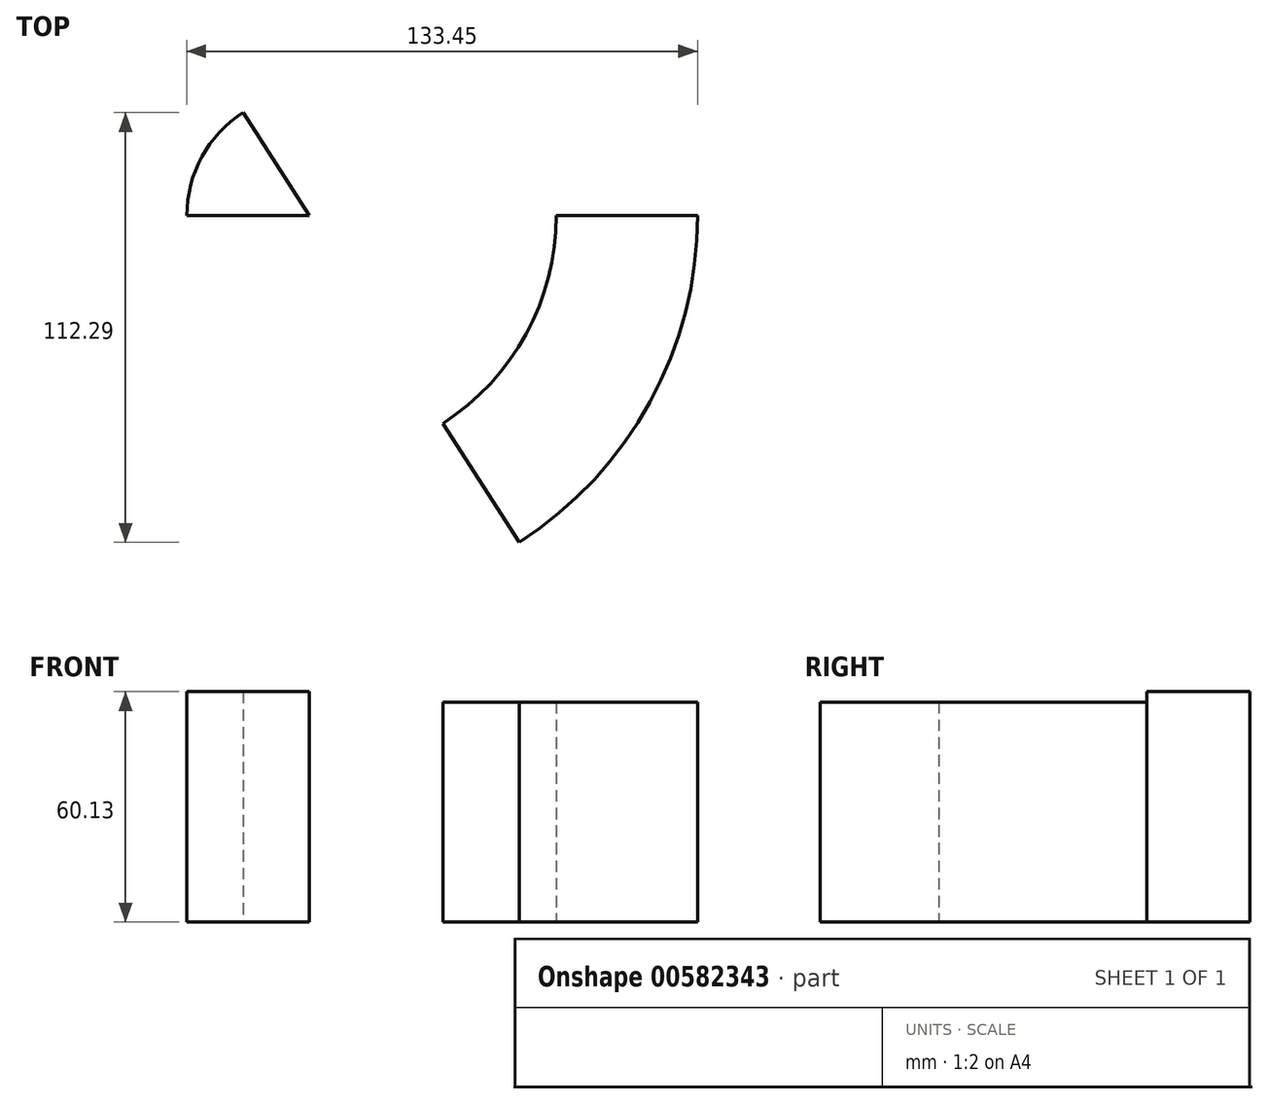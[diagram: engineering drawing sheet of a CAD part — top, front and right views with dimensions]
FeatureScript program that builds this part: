
annotation { "Feature Type Name" : "Feature", "Feature Type Description" : "" }
export const myFeature = defineFeature(function(context is Context, id is Id, definition is map)
    precondition{}
    {
        {
            var Q0;
            Q0=qCreatedBy(makeId("Front.planeOp"),FACE);
            var sketch = newSketch(context, id + "F0", { "sketchPlane" : qUnion([Q0])});
            skLineSegment(sketch, "E0.bottom", {"start": v(-61.35, 60.13) * mm, "end": v(-29.33, 60.13) * mm});
            skLineSegment(sketch, "E0.top", {"start": v(-61.35, 0) * mm, "end": v(-29.33, 0) * mm});
            skLineSegment(sketch, "E0.left", {"start": v(-61.35, 60.13) * mm, "end": v(-61.35, 0) * mm});
            skLineSegment(sketch, "E0.right", {"start": v(-29.33, 60.13) * mm, "end": v(-29.33, 0) * mm});
            skLineSegment(sketch, "E1.bottom", {"start": v(35.2, 57.44) * mm, "end": v(72.1, 57.44) * mm});
            skLineSegment(sketch, "E1.top", {"start": v(35.2, 0) * mm, "end": v(72.1, 0) * mm});
            skLineSegment(sketch, "E1.left", {"start": v(35.2, 57.44) * mm, "end": v(35.2, 0) * mm});
            skLineSegment(sketch, "E1.right", {"start": v(72.1, 57.44) * mm, "end": v(72.1, 0) * mm});
            skSolve(sketch);
        }
        {
            var Q0;
            Q0 = qSketchRegion(id + "F0", true);
            var Q1;
            Q1=sQuery(id+"F0.wireOp",EDGE,"E0.right");
            revolve(context, id + "F1", {"entities" : qUnion([Q0]), "axis" : qUnion([Q1]), "revolveType" : RevolveType.ONE_DIRECTION, "angle" : 1 * radian});
        }
    });
